# Revit family: 1224xxx Atelier 200 (UL)
name_source: partatom
category: Lighting Fixtures
revit_build: Autodesk Revit 2018 (Build: 20170223_1515(x64)
units: mm (PartAtom-declared; Revit-internal decimal feet)

## family parameters
Always vertical = Yes
Cut with Voids When Loaded = No
Host = Ceiling
Light Source = No
OmniClass Number = 23.80.70.11
OmniClass Title = Luminaries for Internal Lighting
Part Type = Normal
Room Calculation Point = No
Round Connector Dimension = Use Diameter
Shared = No

## types (3) — shared parameters
ADA compliant = Not Applicable
Dimmable = Yes
Dimming Method = Lamp Dependent
Driver Included = Not Applicable
Driver Required = No
Efficacy (lm/w) = Lamp Dependent
Electrical Class = 1
Lamp = Incandescent
Length of supplied cable = 1800
Light Source Fixed = No
Location / IP Rating = Dry
Main Material = Metal - Aluminium
Manufacturer URL - Europe and Rest of World = www.astrolighting.com
Manufacturer URL - North America = us.astrolighting.com
Max Drop (pendants) = 2110
Power (Watts) = Lamp Dependent
Product CCT = Lamp Dependent
Product CRI = Lamp Dependent
Product Location = Interior
Product Name = Atelier 200
Product URL = https://us.astrolighting.com
Product Weight (KG) = 2 mm  [stored 0.00656168 ft]

## per-type parameters (varying)
| type | Main Finish | Product Dimensions (MM) | Product SKU |
| Astro Atelier 200 Polished Aluminium | Polished Aluminium | 2110x200x200 | 1224038 |
| Astro Atelier 200 Matt Black | Matt Black | 2110x200x200 | 1224039 |
| Astro Atelier 200 Matt White | Matt White | 2100x200x200 | 1224040 |

note: [stored X ft] marks values corroborated as IEEE doubles in the binary element streams (Revit-internal decimal feet)

## geometry (parser evidence)
native form markers: Sweep x2
no freeform markers — native parametric forms only
